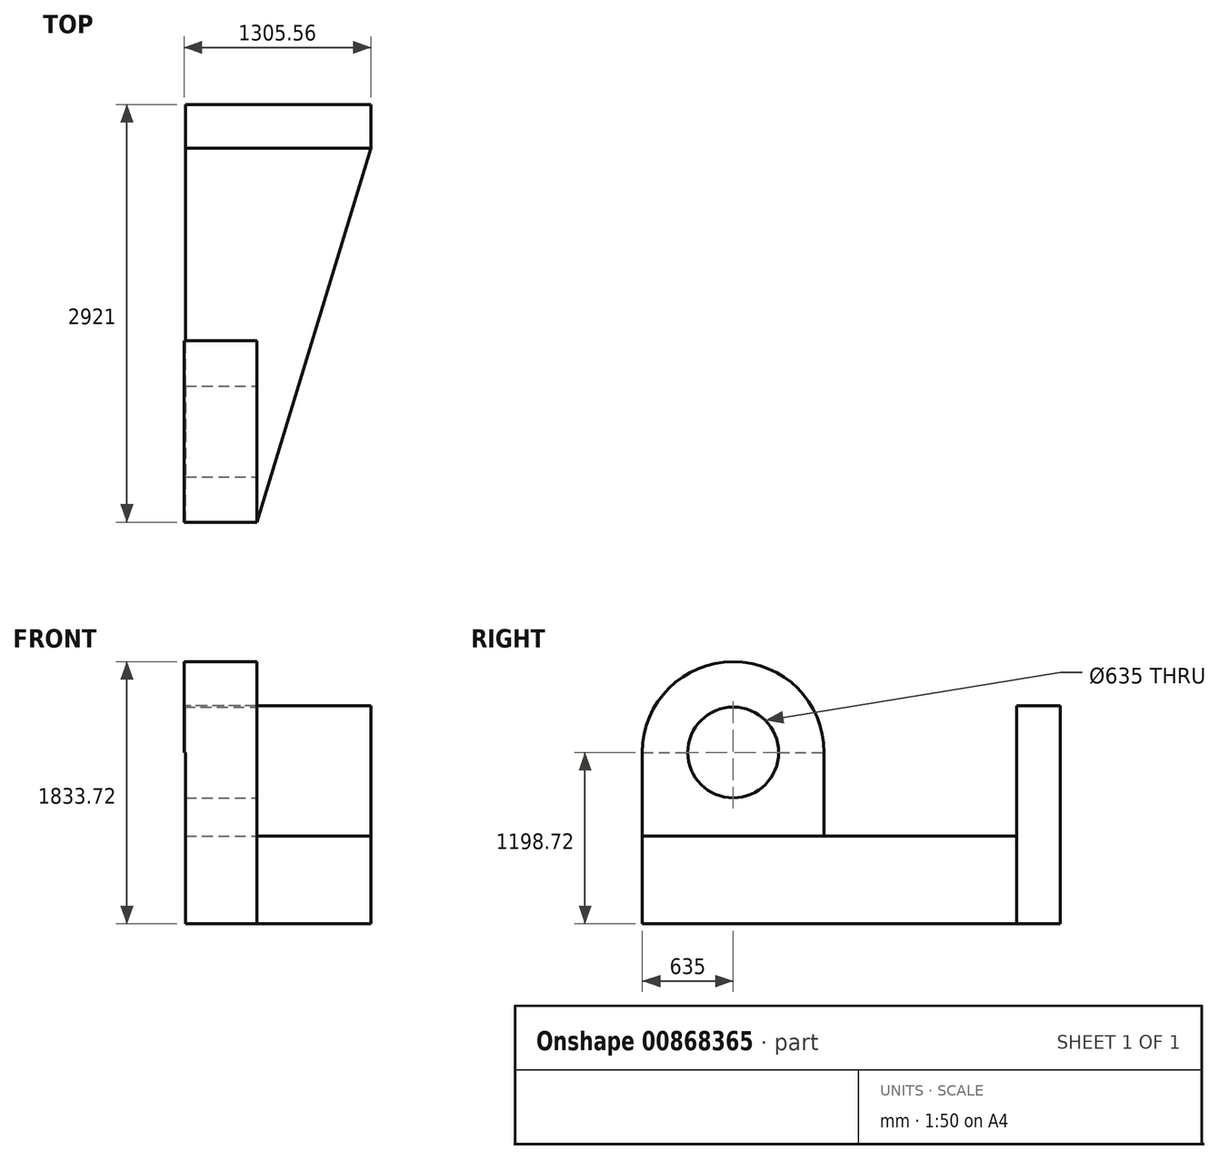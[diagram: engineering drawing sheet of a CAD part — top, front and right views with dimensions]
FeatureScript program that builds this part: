
annotation { "Feature Type Name" : "Feature", "Feature Type Description" : "" }
export const myFeature = defineFeature(function(context is Context, id is Id, definition is map)
    precondition{}
    {
        {
            var Q0;
            Q0=qCreatedBy(makeId("Front.planeOp"),FACE);
            var sketch = newSketch(context, id + "F0", { "sketchPlane" : qUnion([Q0])});
            skLineSegment(sketch, "E0.bottom", {"start": v(0, 0) * mm, "end": v(-1524, 0) * mm});
            skLineSegment(sketch, "E0.top", {"start": v(0, 1524) * mm, "end": v(-1524, 1524) * mm});
            skLineSegment(sketch, "E0.left", {"start": v(0, 0) * mm, "end": v(0, 1524) * mm});
            skLineSegment(sketch, "E0.right", {"start": v(-1524, 0) * mm, "end": v(-1524, 1524) * mm});
            skSolve(sketch);
        }
        {
            var Q0;
            Q0=makeQuery(id+"F0.imprint","IMPRINT",FACE,{"disambiguationData":[TD([[makeQuery(id+"F0.imprint","IMPRINT",EDGE,{"derivedFrom":sQuery(id+"F0.wireOp",EDGE,"E0.bottom")}),-1.0]])]});
            extrude(context, id + "F1", {"entities" : qUnion([Q0]), "depth" : 304.8 * mm, "offsetDistance" : 25.4 * mm});
        }
        {
            var Q0;
            Q0=makeQuery(id+"F1.opExtrude","CAP_FACE",FACE,{"disambiguationData":[OSD([sQuery(id+"F0.wireOp",EDGE,"E0.bottom"),sQuery(id+"F0.wireOp",EDGE,"E0.top"),sQuery(id+"F0.wireOp",EDGE,"E0.left"),sQuery(id+"F0.wireOp",EDGE,"E0.right")])],"isStart":false});
            var sketch = newSketch(context, id + "F2", { "sketchPlane" : qUnion([Q0])});
            skLineSegment(sketch, "E1.bottom", {"start": v(-1524, 0) * mm, "end": v(0, 0) * mm});
            skLineSegment(sketch, "E1.top", {"start": v(-1524, 614.52) * mm, "end": v(0, 614.52) * mm});
            skLineSegment(sketch, "E1.left", {"start": v(-1524, 0) * mm, "end": v(-1524, 614.52) * mm});
            skLineSegment(sketch, "E1.right", {"start": v(0, 0) * mm, "end": v(0, 614.52) * mm});
            skLineSegment(sketch, "E2.bottom", {"start": v(-66.41, 614.52) * mm, "end": v(-1524, 614.52) * mm});
            skLineSegment(sketch, "E2.top", {"start": v(-66.41, 0) * mm, "end": v(-1524, 0) * mm});
            skLineSegment(sketch, "E2.right", {"start": v(-1524, 614.52) * mm, "end": v(-1524, 0) * mm});
            skSolve(sketch);
        }
        {
            var Q0;
            Q0 = qSketchRegion(id + "F2", true);
            extrude(context, id + "F3", {"entities" : qUnion([Q0]), "operationType" : NewBodyOperationType.ADD, "depth" : 2616.2 * mm, "offsetDistance" : 25.4 * mm});
        }
        {
            var Q0;
            Q0=makeQuery(id+"F3.opExtrude","SWEPT_FACE",FACE,{"disambiguationData":[OSD([sQuery(id+"F2.wireOp",EDGE,"E1.top"),sQuery(id+"F2.wireOp",EDGE,"E2.bottom")])]});
            var sketch = newSketch(context, id + "F4", { "sketchPlane" : qUnion([Q0])});
            skLineSegment(sketch, "E3.bottom", {"start": v(-1524, -2921) * mm, "end": v(-1016, -2921) * mm});
            skLineSegment(sketch, "E3.top", {"start": v(-1524, -1651) * mm, "end": v(-1016, -1651) * mm});
            skLineSegment(sketch, "E3.left", {"start": v(-1524, -2921) * mm, "end": v(-1524, -1651) * mm});
            skLineSegment(sketch, "E3.right", {"start": v(-1016, -2921) * mm, "end": v(-1016, -1651) * mm});
            skSolve(sketch);
        }
        {
            var Q0;
            Q0=makeQuery(id+"F4.imprint","IMPRINT",FACE,{"disambiguationData":[TD([[makeQuery(id+"F4.imprint","IMPRINT",EDGE,{"derivedFrom":sQuery(id+"F4.wireOp",EDGE,"E3.bottom")}),1.0]])]});
            extrude(context, id + "F5", {"entities" : qUnion([Q0]), "operationType" : NewBodyOperationType.ADD, "depth" : 584.2 * mm, "offsetDistance" : 25.4 * mm});
        }
        {
            var Q0;
            Q0=makeQuery(id+"F5.opExtrude","SWEPT_FACE",FACE,{"disambiguationData":[OSD([sQuery(id+"F4.wireOp",EDGE,"E3.right")])]});
            extrude(context, id + "F6", {"entities" : qUnion([Q0]), "operationType" : NewBodyOperationType.ADD, "depth" : 218.44 * mm, "offsetDistance" : 25.4 * mm});
        }
        {
            var Q0;
            Q0=makeQuery(id+"F6.opExtrude","CAP_FACE",FACE,{"disambiguationData":[OSD([sQuery(id+"F4.wireOp",EDGE,"E3.right")])],"isStart":false});
            var sketch = newSketch(context, id + "F7", { "sketchPlane" : qUnion([Q0])});
            skCircle(sketch, "E4", {"center": v(-2286, 1198.72) * mm, "radius": 635 * mm});
            skSolve(sketch);
        }
        {
            var Q0;
            {var subQ1=sQuery(id+"F4.wireOp",EDGE,"E3.right");var subQ2=makeQuery(id+"F6.opExtrude","CAP_EDGE",EDGE,{"disambiguationData":[OSD([subQ1]),TDD([makeQuery(id+"F5.opExtrude","CAP_EDGE",EDGE,{"disambiguationData":[OSD([subQ1])],"isStart":false})])],"isStart":false});Q0=makeQuery(id+"F7.imprint","IMPRINT",FACE,{"disambiguationData":[TD([[makeQuery(id+"F7.imprint","IMPRINT",EDGE,{"derivedFrom":subQ2}),1.0]])]});}
            extrude(context, id + "F8", {"entities" : qUnion([Q0]), "operationType" : NewBodyOperationType.ADD, "oppositeDirection" : true, "depth" : 508 * mm, "offsetDistance" : 25.4 * mm});
        }
        {
            var Q0;
            {var subQ0=sQuery(id+"F4.wireOp",EDGE,"E3.right");Q0=makeQuery(id+"F8.boolean.opBoolean","MERGE",FACE,{"derivedFrom":[makeQuery(id+"F6.opExtrude","CAP_FACE",FACE,{"disambiguationData":[OSD([subQ0])],"isStart":false}),makeQuery(id+"F8.opExtrude","CAP_FACE",FACE,{"disambiguationData":[OSD([subQ0,sQuery(id+"F7.wireOp",EDGE,"E4")])],"isStart":true})]});}
            var sketch = newSketch(context, id + "F9", { "sketchPlane" : qUnion([Q0])});
            skCircle(sketch, "E5", {"center": v(-2286, 1198.72) * mm, "radius": 317.5 * mm});
            skSolve(sketch);
        }
        {
            var Q0;
            Q0=makeQuery(id+"F9.imprint","IMPRINT",FACE,{"disambiguationData":[TD([[makeQuery(id+"F9.imprint","IMPRINT",EDGE,{"derivedFrom":sQuery(id+"F9.wireOp",EDGE,"E5")}),1.0]])]});
            extrude(context, id + "F10", {"entities" : qUnion([Q0]), "operationType" : NewBodyOperationType.REMOVE, "oppositeDirection" : true, "depth" : 508 * mm, "offsetDistance" : 25.4 * mm});
        }
        {
            var Q0;
            Q0=makeQuery(id+"F5.boolean.opBoolean","MERGE",FACE,{"derivedFrom":[makeQuery(id+"F3.boolean.opBoolean","MERGE",FACE,{"derivedFrom":[makeQuery(id+"F1.opExtrude","SWEPT_FACE",FACE,{"disambiguationData":[OSD([sQuery(id+"F0.wireOp",EDGE,"E0.right")])]}),makeQuery(id+"F3.opExtrude","SWEPT_FACE",FACE,{"disambiguationData":[OSD([sQuery(id+"F2.wireOp",EDGE,"E2.right")])]})]}),makeQuery(id+"F5.opExtrude","SWEPT_FACE",FACE,{"disambiguationData":[OSD([sQuery(id+"F4.wireOp",EDGE,"E3.left")])]})]});
            extrude(context, id + "F11", {"entities" : qUnion([Q0]), "operationType" : NewBodyOperationType.REMOVE, "oppositeDirection" : true, "depth" : 228.6 * mm, "offsetDistance" : 25.4 * mm});
        }
        {
            var Q0;
            Q0=makeQuery(id+"F3.opExtrude","SWEPT_FACE",FACE,{"disambiguationData":[OSD([sQuery(id+"F2.wireOp",EDGE,"E1.top"),sQuery(id+"F2.wireOp",EDGE,"E2.bottom")])]});
            var sketch = newSketch(context, id + "F12", { "sketchPlane" : qUnion([Q0])});
            skLineSegment(sketch, "E6", {"start": v(-797.56, -2921) * mm, "end": v(0, -304.8) * mm});
            skSolve(sketch);
        }
        {
            var Q0;
            Q0=makeQuery(id+"F12.imprint","IMPRINT",FACE,{"disambiguationData":[TD([[makeQuery(id+"F12.imprint","IMPRINT",EDGE,{"derivedFrom":sQuery(id+"F12.wireOp",EDGE,"E6")}),-1.0]])]});
            extrude(context, id + "F13", {"entities" : qUnion([Q0]), "operationType" : NewBodyOperationType.REMOVE, "oppositeDirection" : true, "depth" : 1165.86 * mm, "offsetDistance" : 25.4 * mm});
        }
    });
